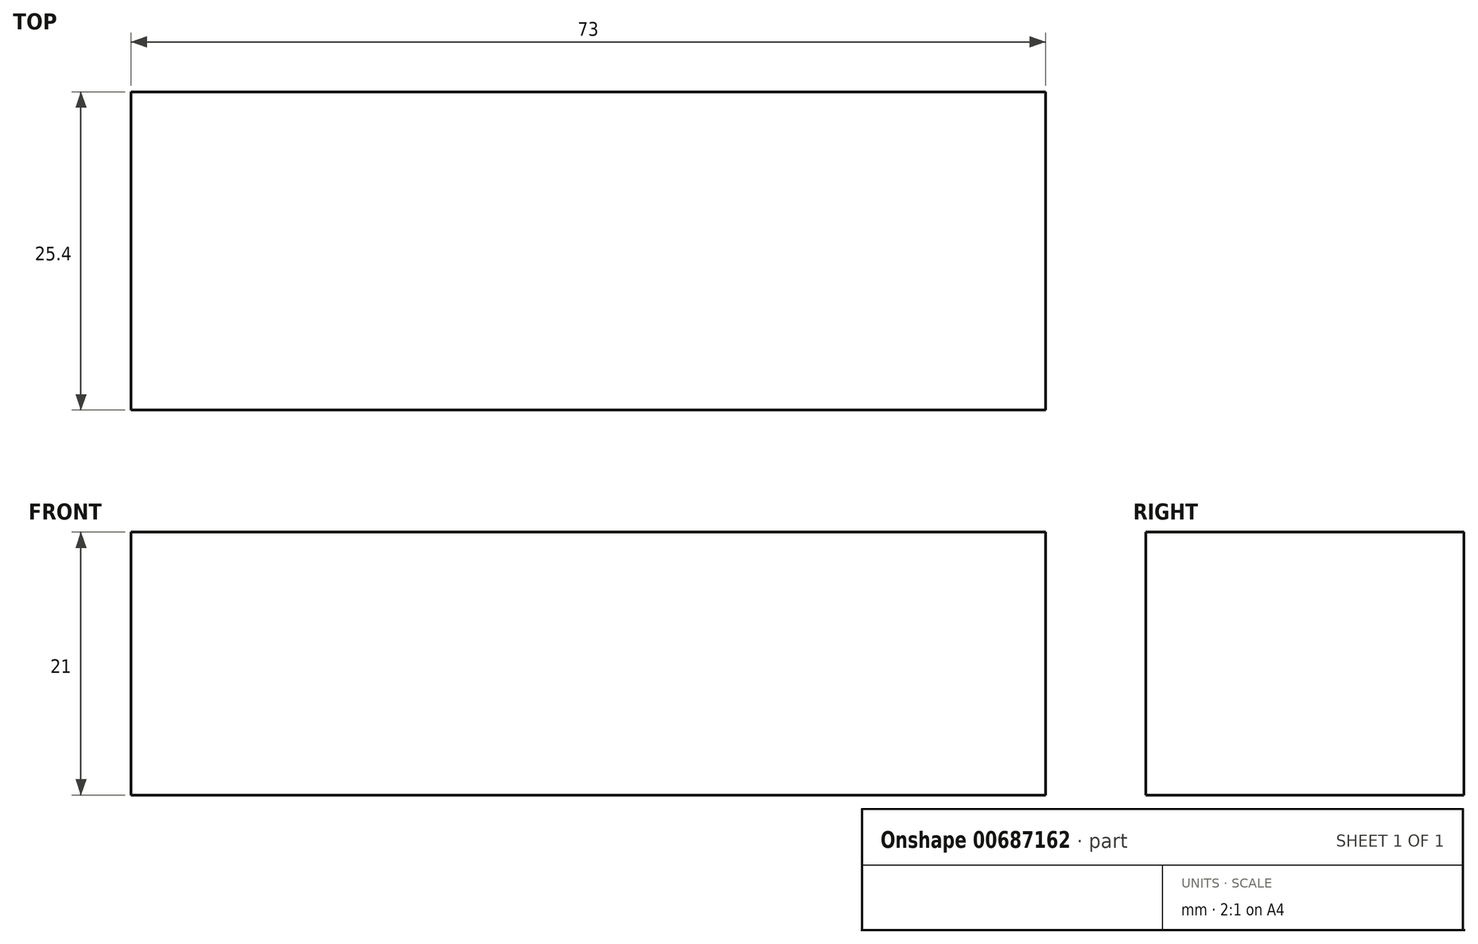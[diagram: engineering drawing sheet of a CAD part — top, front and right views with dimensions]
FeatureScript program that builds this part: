
annotation { "Feature Type Name" : "Feature", "Feature Type Description" : "" }
export const myFeature = defineFeature(function(context is Context, id is Id, definition is map)
    precondition{}
    {
        {
            var Q0;
            Q0=qCreatedBy(makeId("Front.planeOp"),FACE);
            var sketch = newSketch(context, id + "F0", { "sketchPlane" : qUnion([Q0])});
            skLineSegment(sketch, "E0.bottom", {"start": v(-36.5, 10.5) * mm, "end": v(36.5, 10.5) * mm});
            skLineSegment(sketch, "E0.top", {"start": v(-36.5, -10.5) * mm, "end": v(36.5, -10.5) * mm});
            skLineSegment(sketch, "E0.left", {"start": v(-36.5, 10.5) * mm, "end": v(-36.5, -10.5) * mm});
            skLineSegment(sketch, "E0.right", {"start": v(36.5, 10.5) * mm, "end": v(36.5, -10.5) * mm});
            skPoint(sketch, "E0.middle", {"position": v(0, 0) * mm});
            skSolve(sketch);
        }
        {
            var Q0;
            Q0 = qSketchRegion(id + "F0", true);
            extrude(context, id + "F1", {"entities" : qUnion([Q0]), "depth" : 25.4 * mm, "offsetDistance" : 25.4 * mm});
        }
    });
